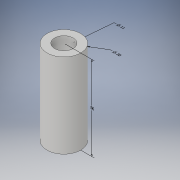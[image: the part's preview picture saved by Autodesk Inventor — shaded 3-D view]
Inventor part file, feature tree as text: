
AUTODESK INVENTOR PART (.ipt)
format: ipt  version: 2018 (Build 220112000, 112)  size: 109,568 bytes
history: native  units: in
note: dims shown in document units (in); Inventor stores cm internally (conversion verified against a paired STEP export)
features: other x4, sketch x2, extrude x1, hole x1
ambient origin geometry x8: Origin, YZ Plane, XZ Plane, XY Plane, X Axis, Y Axis, Z Axis, Center Point
bodies: Solid1 (feature_tree)
feature tree (8):
  other  "Annotations"
  extrude  "Extrusion1"  Depth=0.5in TaperAngle=0.0deg
  hole  "Hole1"  [1 undecoded]
  sketch  "Sketch1"  dims[d0=0.2in d1=0.5in d2=0.0in]
  sketch  "Sketch2"  dims[d3=0.11in d4=0.11in d5=0.75in d6=0.375in d7=0.25in d8=0.5635in d9=1.0in d10=0.8108in d11=1.9418in d12=0.0149in d13=0.3261in d14=0.11in d15=1.452in d16=0.2in d17=0.5in]
  other  "Diameter Dimension 1"
  other  "Diameter Dimension 2"
  other  "Linear Dimension 1"
note: 1 required parameter value undecoded (feature->parameter linkage not recoverable at this tier; creation-order binding heuristic only, values carry confidence <= 0.55)
